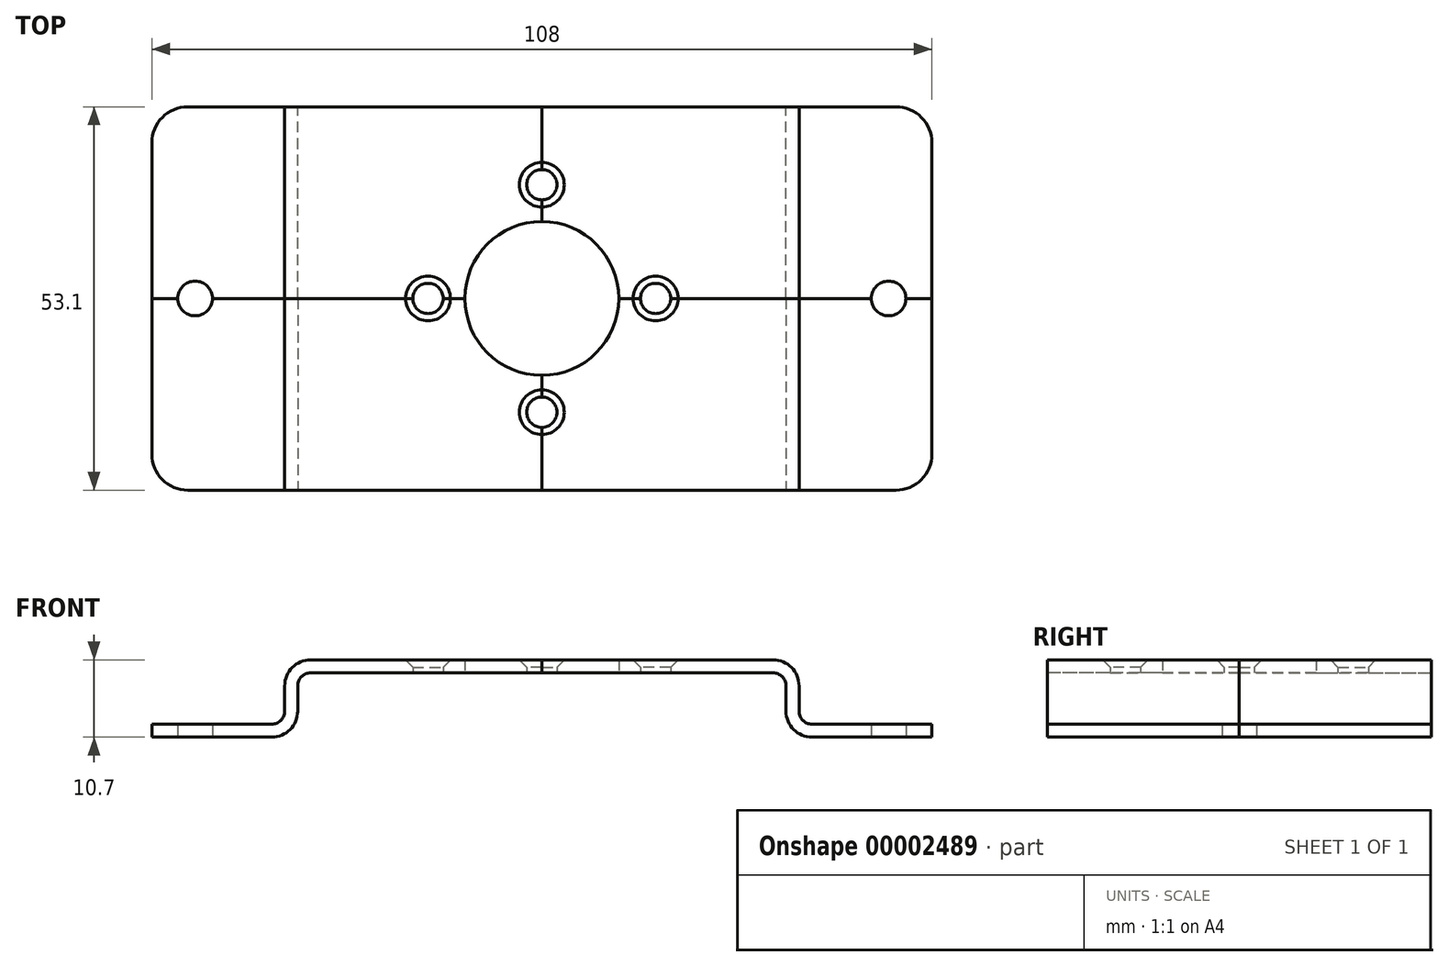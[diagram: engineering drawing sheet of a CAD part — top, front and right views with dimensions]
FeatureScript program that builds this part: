
annotation { "Feature Type Name" : "Feature", "Feature Type Description" : "" }
export const myFeature = defineFeature(function(context is Context, id is Id, definition is map)
    precondition{}
    {
        {
            var Q0;
            Q0=qCreatedBy(makeId("Top.planeOp"),FACE);
            var sketch = newSketch(context, id + "F0", { "sketchPlane" : qUnion([Q0])});
            skLineSegment(sketch, "E0", {"start": v(-128.05, 0) * mm, "end": v(128.05, 0) * mm, "construction": true});
            skLineSegment(sketch, "E1", {"start": v(0, 0) * mm, "end": v(0, 26.55) * mm, "construction": true});
            skLineSegment(sketch, "E2", {"start": v(54, 0) * mm, "end": v(54, 26.55) * mm});
            skLineSegment(sketch, "E3", {"start": v(54, 26.55) * mm, "end": v(0, 26.55) * mm});
            skLineSegment(sketch, "E4.0", {"start": v(48, 0) * mm, "end": v(48, 4.35) * mm, "construction": true});
            skArc(sketch, "E5", {"start": v(50.4, 0) * mm, "mid": v(48, 2.4) * mm, "end": v(45.6, 0) * mm});
            skArc(sketch, "E6", {"start": v(10.65, 0) * mm, "mid": v(7.53, 7.53) * mm, "end": v(0, 10.65) * mm});
            skArc(sketch, "E7", {"start": v(0, 13.65) * mm, "mid": v(2.1, 15.75) * mm, "end": v(0, 17.85) * mm});
            skLineSegment(sketch, "E8", {"start": v(0, 0) * mm, "end": v(7.53, 7.53) * mm, "construction": true});
            skArc(sketch, "E9.0.MirrorC", {"start": v(13.65, 0) * mm, "mid": v(15.75, 2.1) * mm, "end": v(17.85, 0) * mm});
            skLineSegment(sketch, "E10", {"start": v(0, 10.65) * mm, "end": v(0, 13.65) * mm});
            skLineSegment(sketch, "E11", {"start": v(0, 26.55) * mm, "end": v(0, 17.85) * mm});
            skLineSegment(sketch, "E12", {"start": v(13.65, 0) * mm, "end": v(10.65, 0) * mm});
            skLineSegment(sketch, "E13", {"start": v(17.85, 0) * mm, "end": v(45.6, 0) * mm});
            skLineSegment(sketch, "E14", {"start": v(50.4, 0) * mm, "end": v(54, 0) * mm});
            skSolve(sketch);
        }
        {
            var Q0;
            Q0=makeQuery(id+"F0.imprint","IMPRINT",FACE,{"disambiguationData":[TD([[makeQuery(id+"F0.imprint","IMPRINT",EDGE,{"derivedFrom":sQuery(id+"F0.wireOp",EDGE,"E2")}),1.0]])]});
            extrude(context, id + "F1", {"entities" : qUnion([Q0]), "depth" : 10.7 * mm});
        }
        {
            var Q0;
            Q0=makeQuery(id+"F1.opExtrude","SWEPT_FACE",FACE,{"disambiguationData":[OSD([sQuery(id+"F0.wireOp",EDGE,"E3")])]});
            var sketch = newSketch(context, id + "F2", { "sketchPlane" : qUnion([Q0])});
            skLineSegment(sketch, "E15.0", {"start": v(-54, 1.8) * mm, "end": v(-54, 0) * mm});
            skLineSegment(sketch, "E15.1", {"start": v(-32, 10.7) * mm, "end": v(0, 10.7) * mm});
            skLineSegment(sketch, "E15.2", {"start": v(-54, 0) * mm, "end": v(-37.4, 0) * mm});
            skLineSegment(sketch, "E15.3", {"start": v(0, 10.7) * mm, "end": v(0, 8.9) * mm});
            skLineSegment(sketch, "E16.0", {"start": v(-33.8, 7.1) * mm, "end": v(-33.8, 3.6) * mm});
            skLineSegment(sketch, "E17.0", {"start": v(-35.6, 7.1) * mm, "end": v(-35.6, 3.6) * mm});
            skLineSegment(sketch, "E18.0", {"start": v(-54, 1.8) * mm, "end": v(-37.4, 1.8) * mm});
            skLineSegment(sketch, "E19.0", {"start": v(-32, 8.9) * mm, "end": v(0, 8.9) * mm});
            skPoint(sketch, "E20.orphan", {"position": v(0, 0) * mm});
            skPoint(sketch, "E21.end.orphan", {"position": v(0, 5.35) * mm});
            skPoint(sketch, "E22.orphan", {"position": v(-54, 5.35) * mm});
            skArc(sketch, "E23", {"start": v(-32, 10.7) * mm, "mid": v(-34.55, 9.65) * mm, "end": v(-35.6, 7.1) * mm});
            skArc(sketch, "E24", {"start": v(-32, 8.9) * mm, "mid": v(-33.27, 8.37) * mm, "end": v(-33.8, 7.1) * mm});
            skArc(sketch, "E25", {"start": v(-37.4, 0) * mm, "mid": v(-34.85, 1.05) * mm, "end": v(-33.8, 3.6) * mm});
            skArc(sketch, "E26", {"start": v(-37.4, 1.8) * mm, "mid": v(-36.13, 2.33) * mm, "end": v(-35.6, 3.6) * mm});
            skSolve(sketch);
        }
        {
            var Q0;
            {var subQ2=sQuery(id+"F2.wireOp",EDGE,"E17.0");Q0=makeQuery(id+"F2.imprint","IMPRINT",FACE,{"disambiguationData":[TD([[makeQuery(id+"F2.imprint","IMPRINT",EDGE,{"derivedFrom":subQ2}),-1.0]])]});}
            var Q1;
            {var subQ2=sQuery(id+"F2.wireOp",EDGE,"E16.0");Q1=makeQuery(id+"F2.imprint","IMPRINT",FACE,{"disambiguationData":[TD([[makeQuery(id+"F2.imprint","IMPRINT",EDGE,{"derivedFrom":subQ2}),1.0]])]});}
            extrude(context, id + "F3", {"entities" : qUnion([Q0, Q1]), "operationType" : NewBodyOperationType.REMOVE, "endBound" : BoundingType.UP_TO_NEXT, "oppositeDirection" : true, "depth" : 25 * mm});
        }
        {
            var Q0;
            Q0=makeQuery(id+"F1.opExtrude","CAP_EDGE",EDGE,{"disambiguationData":[OSD([sQuery(id+"F0.wireOp",EDGE,"E7")])],"isStart":false});
            var Q1;
            Q1=makeQuery(id+"F1.opExtrude","CAP_EDGE",EDGE,{"disambiguationData":[OSD([sQuery(id+"F0.wireOp",EDGE,"E9.0.MirrorC")])],"isStart":false});
            chamfer(context, id + "F4", {"entities" : qUnion([Q0, Q1]), "width" : 1 * mm, "tangentPropagation" : true});
        }
        {
            var Q0;
            Q0=makeQuery(id+"F1.opExtrude","SWEPT_EDGE",EDGE,{"disambiguationData":[OSD([sQuery(id+"F0.wireOp",EDGE,"E2"),sQuery(id+"F0.wireOp",EDGE,"E3")])]});
            fillet(context, id + "F5", {"entities" : qUnion([Q0]), "radius" : 5 * mm, "tangentPropagation" : true, "allowEdgeOverflow" : false});
        }
        {
            var Q0;
            Q0=makeQuery(id+"F1.opExtrude","SWEPT_BODY",BODY,{"disambiguationData":[OSD([sQuery(id+"F0.wireOp",EDGE,"E2"),sQuery(id+"F0.wireOp",EDGE,"E3"),sQuery(id+"F0.wireOp",EDGE,"E5"),sQuery(id+"F0.wireOp",EDGE,"E6"),sQuery(id+"F0.wireOp",EDGE,"E7"),sQuery(id+"F0.wireOp",EDGE,"E9.0.MirrorC"),sQuery(id+"F0.wireOp",EDGE,"E10"),sQuery(id+"F0.wireOp",EDGE,"E11"),sQuery(id+"F0.wireOp",EDGE,"E12"),sQuery(id+"F0.wireOp",EDGE,"E13"),sQuery(id+"F0.wireOp",EDGE,"E14")])]});
            var Q1;
            Q1=makeQuery(id+"F1.opExtrude","SWEPT_FACE",FACE,{"disambiguationData":[OSD([sQuery(id+"F0.wireOp",EDGE,"E13")])]});
            mirror(context, id + "F6", {"entities" : qUnion([Q0]), "mirrorPlane" : qUnion([Q1])});
        }
        {
            var Q0;
            Q0=makeQuery(id+"F1.opExtrude","SWEPT_BODY",BODY,{"disambiguationData":[OSD([sQuery(id+"F0.wireOp",EDGE,"E2"),sQuery(id+"F0.wireOp",EDGE,"E3"),sQuery(id+"F0.wireOp",EDGE,"E5"),sQuery(id+"F0.wireOp",EDGE,"E6"),sQuery(id+"F0.wireOp",EDGE,"E7"),sQuery(id+"F0.wireOp",EDGE,"E9.0.MirrorC"),sQuery(id+"F0.wireOp",EDGE,"E10"),sQuery(id+"F0.wireOp",EDGE,"E11"),sQuery(id+"F0.wireOp",EDGE,"E12"),sQuery(id+"F0.wireOp",EDGE,"E13"),sQuery(id+"F0.wireOp",EDGE,"E14")])]});
            var Q1;
            Q1=makeQuery(id+"F6.opPattern","COPY",BODY,{"derivedFrom":makeQuery(id+"F1.opExtrude","SWEPT_BODY",BODY,{"disambiguationData":[OSD([sQuery(id+"F0.wireOp",EDGE,"E2"),sQuery(id+"F0.wireOp",EDGE,"E3"),sQuery(id+"F0.wireOp",EDGE,"E5"),sQuery(id+"F0.wireOp",EDGE,"E6"),sQuery(id+"F0.wireOp",EDGE,"E7"),sQuery(id+"F0.wireOp",EDGE,"E9.0.MirrorC"),sQuery(id+"F0.wireOp",EDGE,"E10"),sQuery(id+"F0.wireOp",EDGE,"E11"),sQuery(id+"F0.wireOp",EDGE,"E12"),sQuery(id+"F0.wireOp",EDGE,"E13"),sQuery(id+"F0.wireOp",EDGE,"E14")])]}),"instanceName":"1"});
            var Q2;
            Q2=makeQuery(id+"F1.opExtrude","SWEPT_FACE",FACE,{"disambiguationData":[OSD([sQuery(id+"F0.wireOp",EDGE,"E11")])]});
            mirror(context, id + "F7", {"entities" : qUnion([Q0, Q1]), "mirrorPlane" : qUnion([Q2])});
        }
    });
